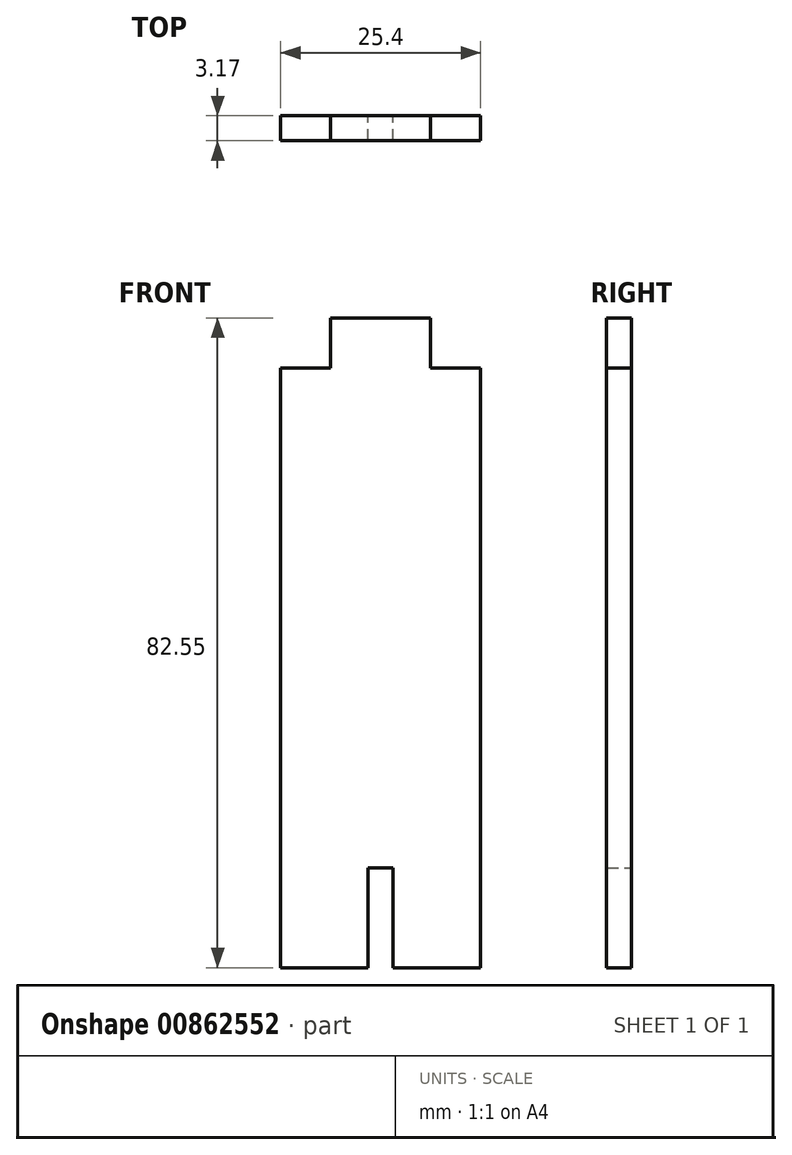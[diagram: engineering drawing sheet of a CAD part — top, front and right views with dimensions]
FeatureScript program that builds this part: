
annotation { "Feature Type Name" : "Feature", "Feature Type Description" : "" }
export const myFeature = defineFeature(function(context is Context, id is Id, definition is map)
    precondition{}
    {
        {
            var Q0;
            Q0=qCreatedBy(makeId("Front.planeOp"),FACE);
            var sketch = newSketch(context, id + "F0", { "sketchPlane" : qUnion([Q0])});
            skLineSegment(sketch, "E0.top", {"start": v(12.7, -12.7) * mm, "end": v(1.59, -12.7) * mm});
            skPoint(sketch, "E0.middle", {"position": v(0, 0) * mm});
            skLineSegment(sketch, "E1", {"start": v(0, 0) * mm, "end": v(1.59, 0) * mm});
            skLineSegment(sketch, "E2", {"start": v(1.59, 0) * mm, "end": v(1.59, -12.7) * mm});
            skLineSegment(sketch, "E3.MirrorCS", {"start": v(-1.59, 0) * mm, "end": v(-1.59, -12.7) * mm});
            skLineSegment(sketch, "E4.MirrorCS", {"start": v(0, 0) * mm, "end": v(-1.59, 0) * mm});
            skLineSegment(sketch, "E5.trimOffspring", {"start": v(-1.59, -12.7) * mm, "end": v(-12.7, -12.7) * mm});
            skLineSegment(sketch, "E6", {"start": v(12.7, -12.7) * mm, "end": v(12.7, 63.5) * mm});
            skLineSegment(sketch, "E7", {"start": v(-12.7, -12.7) * mm, "end": v(-12.7, 63.5) * mm});
            skLineSegment(sketch, "E8", {"start": v(-6.35, 69.85) * mm, "end": v(6.35, 69.85) * mm});
            skLineSegment(sketch, "E9", {"start": v(-6.35, 69.85) * mm, "end": v(-6.35, 63.5) * mm});
            skLineSegment(sketch, "E10.MirrorCS", {"start": v(6.35, 69.85) * mm, "end": v(6.35, 63.5) * mm});
            skLineSegment(sketch, "E11", {"start": v(6.35, 63.5) * mm, "end": v(12.7, 63.5) * mm});
            skLineSegment(sketch, "E12", {"start": v(-6.35, 63.5) * mm, "end": v(-12.7, 63.5) * mm});
            skSolve(sketch);
        }
        {
            var Q0;
            Q0 = qSketchRegion(id + "F0", true);
            extrude(context, id + "F1", {"entities" : qUnion([Q0]), "depth" : 3.17 * mm, "offsetDistance" : 25.4 * mm});
        }
    });
